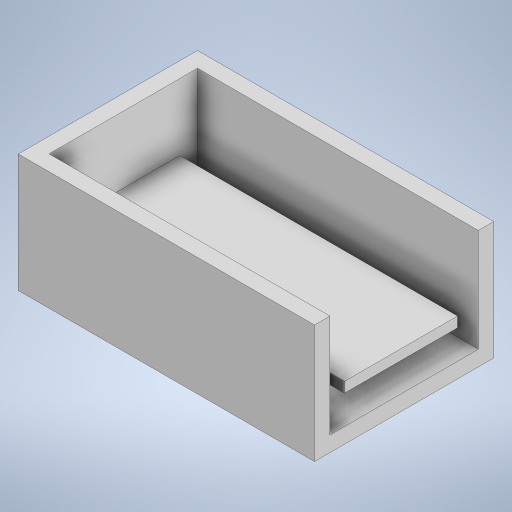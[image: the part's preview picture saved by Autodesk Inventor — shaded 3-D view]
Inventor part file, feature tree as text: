
AUTODESK INVENTOR PART (.ipt)
format: ipt  version: 2024 (Build 280153000, 153)  size: 225,280 bytes
history: native  units: in
note: dims shown in document units (in); Inventor stores cm internally (conversion verified against a paired STEP export)
features: extrude x4, sketch x3
ambient origin geometry x8: Origin, YZ Plane, XZ Plane, XY Plane, X Axis, Y Axis, Z Axis, Center Point
bodies: Solid1 (feature_tree)
feature tree (7):
  sketch  "Sketch1"  dims[d0=1.1358in d1=2.0315in]
  extrude  "Extrusion1"  Depth=2.0315in
  extrude  "Extrusion2"  Depth=0.1181in TaperAngle=0.0deg
  extrude  "Extrusion3"  Depth=0.9055in TaperAngle=0.0deg
  extrude  "Extrusion4"  Depth=0.1969in
  sketch  "Sketch2"  dims[d2=0.1181in d3=0.1181in d4=0.0in]
  sketch  "Sketch3"  dims[d5=0.9055in d6=0.0in d7=0.9055in d8=0.0in d9=0.1969in d10=0.4331in d11=0.4331in d12=0.0787in d13=2.126in d14=0.0in]
